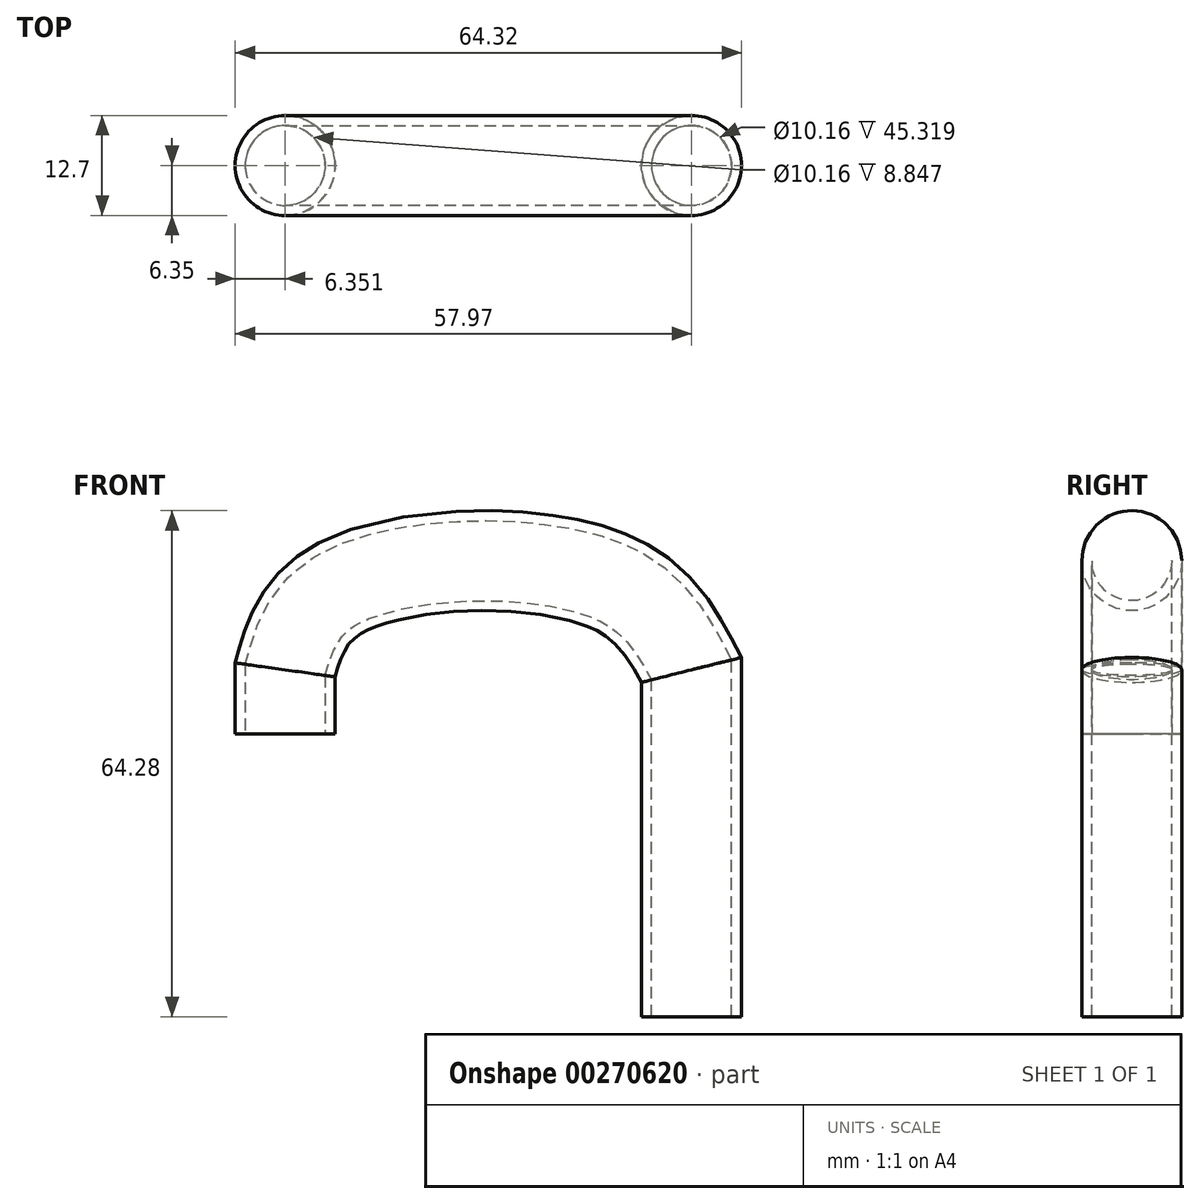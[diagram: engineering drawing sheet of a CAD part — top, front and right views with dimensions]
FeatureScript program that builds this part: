
annotation { "Feature Type Name" : "Feature", "Feature Type Description" : "" }
export const myFeature = defineFeature(function(context is Context, id is Id, definition is map)
    precondition{}
    {
        {
            var Q0;
            Q0=qCreatedBy(makeId("Top.planeOp"),FACE);
            var sketch = newSketch(context, id + "F0", { "sketchPlane" : qUnion([Q0])});
            skCircle(sketch, "E0", {"center": v(0, 0) * mm, "radius": 6.35 * mm});
            skCircle(sketch, "E1", {"center": v(0, 0) * mm, "radius": 5.08 * mm});
            skSolve(sketch);
        }
        {
            var Q0;
            Q0=qCreatedBy(makeId("Front.planeOp"),FACE);
            var sketch = newSketch(context, id + "F1", { "sketchPlane" : qUnion([Q0])});
            skLineSegment(sketch, "E2", {"start": v(0, 0) * mm, "end": v(0, 44.06) * mm});
            skFitSpline(sketch, "E3", {"points": [v(0, 44.06) * mm, v(-10.88, 55.5) * mm, v(-44.8, 54.38) * mm, v(-51.62, 44.06) * mm], "startDerivative": vector(-23.68, 44.9) * mm, "endDerivative": vector(-12.56, -44.14) * mm});
            skLineSegment(sketch, "E4", {"start": v(-51.62, 44.06) * mm, "end": v(-51.62, 35.92) * mm});
            skSolve(sketch);
        }
        {
            var Q0;
            Q0=makeQuery(id+"F0.imprint","IMPRINT",FACE,{"disambiguationData":[TD([[makeQuery(id+"F0.imprint","IMPRINT",EDGE,{"derivedFrom":sQuery(id+"F0.wireOp",EDGE,"E0")}),1.0]])]});
            var Q1;
            Q1=sQuery(id+"F1.wireOp",EDGE,"E2");
            var Q2;
            Q2=sQuery(id+"F1.wireOp",EDGE,"E3");
            var Q3;
            Q3=sQuery(id+"F1.wireOp",EDGE,"E4");
            sweep(context, id + "F2", {"profiles" : qUnion([Q0]), "path" : qUnion([Q1, Q2, Q3])});
        }
    });
